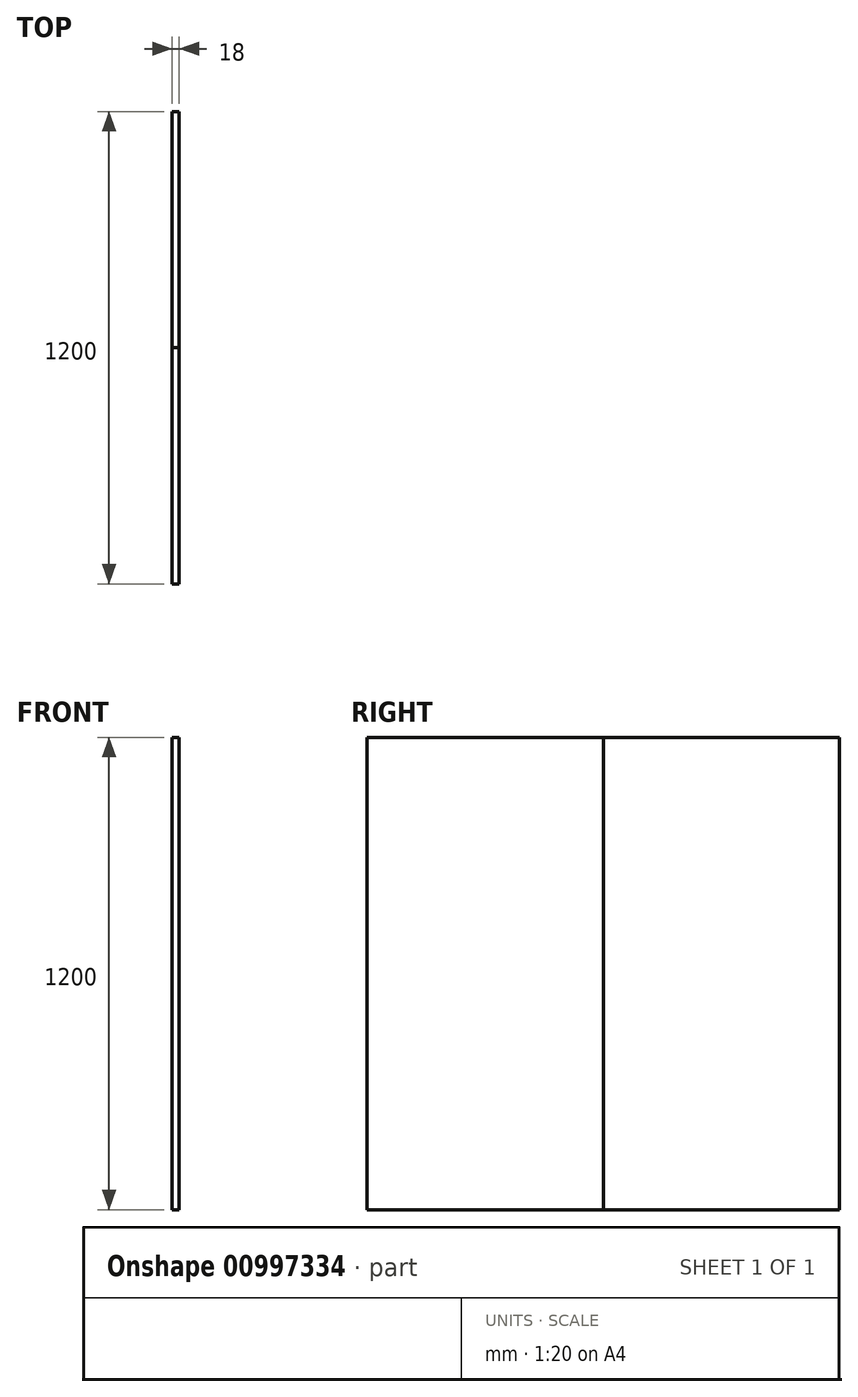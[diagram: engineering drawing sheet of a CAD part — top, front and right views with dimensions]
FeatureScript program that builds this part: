
annotation { "Feature Type Name" : "Feature", "Feature Type Description" : "" }
export const myFeature = defineFeature(function(context is Context, id is Id, definition is map)
    precondition{}
    {
        {
            var Q0;
            Q0=qCreatedBy(makeId("Right.planeOp"),FACE);
            var sketch = newSketch(context, id + "F0", { "sketchPlane" : qUnion([Q0])});
            skLineSegment(sketch, "E0.bottom", {"start": v(0, 0) * mm, "end": v(600, 0) * mm});
            skLineSegment(sketch, "E0.top", {"start": v(0, 1200) * mm, "end": v(600, 1200) * mm});
            skLineSegment(sketch, "E0.left", {"start": v(0, 0) * mm, "end": v(0, 1200) * mm});
            skLineSegment(sketch, "E0.right", {"start": v(600, 0) * mm, "end": v(600, 1200) * mm});
            skLineSegment(sketch, "E1.bottom", {"start": v(0, 0) * mm, "end": v(-600, 0) * mm});
            skLineSegment(sketch, "E1.top", {"start": v(0, 1200) * mm, "end": v(-600, 1200) * mm});
            skLineSegment(sketch, "E1.right", {"start": v(-600, 0) * mm, "end": v(-600, 1200) * mm});
            skSolve(sketch);
        }
        {
            var Q0;
            Q0=makeQuery(id+"F0.imprint","IMPRINT",FACE,{"disambiguationData":[TD([[makeQuery(id+"F0.imprint","IMPRINT",EDGE,{"derivedFrom":sQuery(id+"F0.wireOp",EDGE,"E1.bottom")}),-1.0]])]});
            extrude(context, id + "F1", {"entities" : qUnion([Q0]), "oppositeDirection" : true, "depth" : 18 * mm, "offsetDistance" : 25 * mm});
        }
        {
            var Q0;
            Q0=makeQuery(id+"F0.imprint","IMPRINT",FACE,{"disambiguationData":[TD([[makeQuery(id+"F0.imprint","IMPRINT",EDGE,{"derivedFrom":sQuery(id+"F0.wireOp",EDGE,"E0.bottom")}),1.0]])]});
            extrude(context, id + "F2", {"entities" : qUnion([Q0]), "oppositeDirection" : true, "depth" : 18 * mm, "offsetDistance" : 25 * mm});
        }
    });
